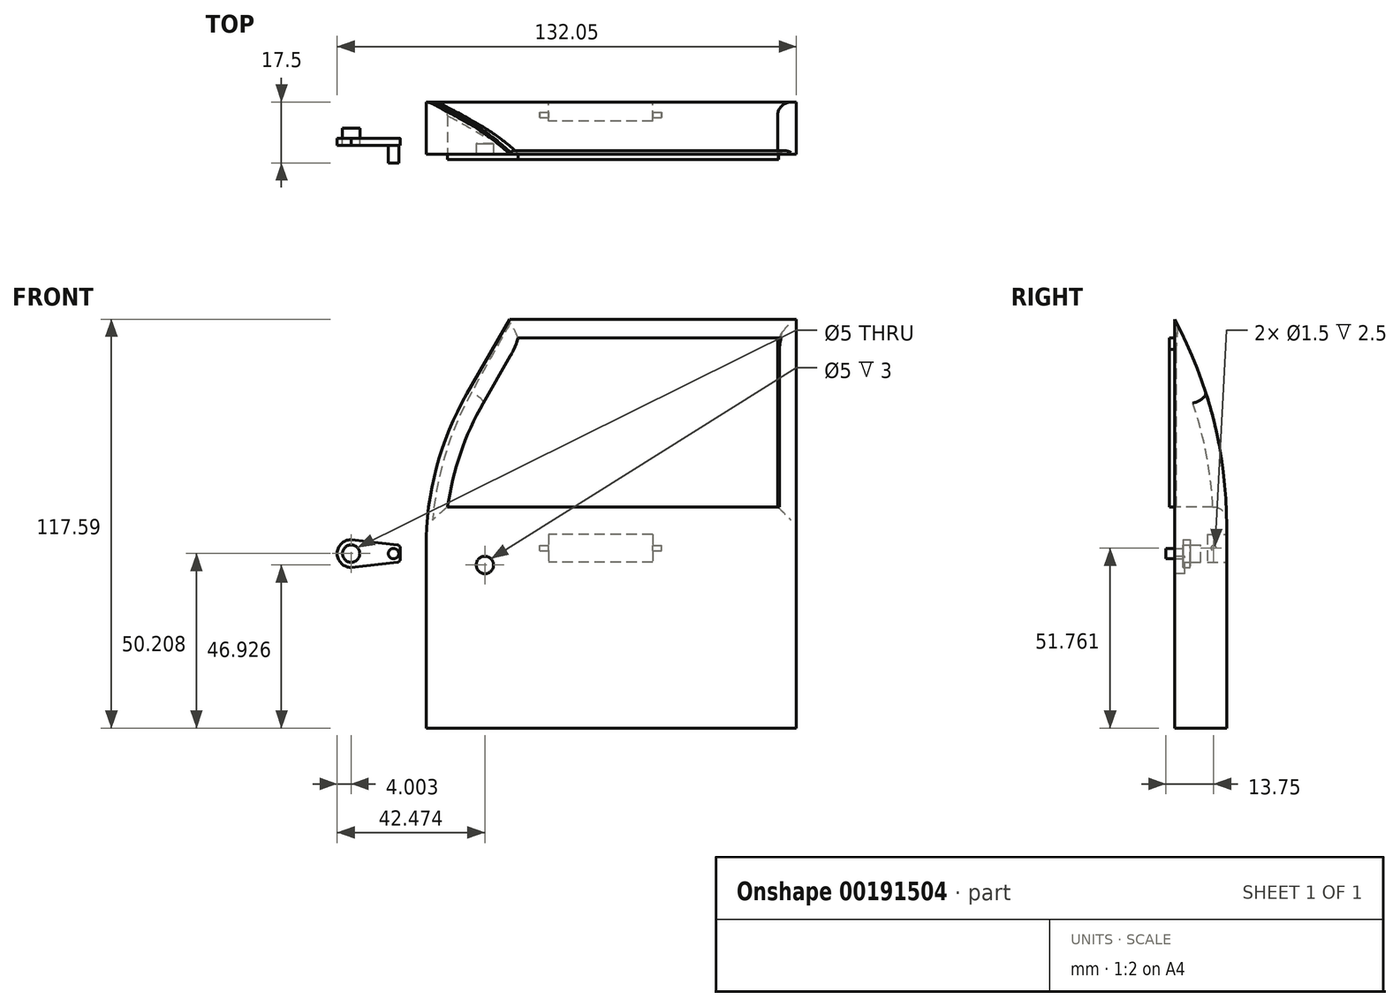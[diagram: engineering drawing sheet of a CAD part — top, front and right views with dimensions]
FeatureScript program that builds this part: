
annotation { "Feature Type Name" : "Feature", "Feature Type Description" : "" }
export const myFeature = defineFeature(function(context is Context, id is Id, definition is map)
    precondition{}
    {
        {
            var Q0;
            Q0=qCreatedBy(makeId("Front.planeOp"),FACE);
            var sketch = newSketch(context, id + "F0", { "sketchPlane" : qUnion([Q0])});
            skLineSegment(sketch, "E0.bottom", {"start": v(-26.16, 41.9) * mm, "end": v(56.28, 41.9) * mm});
            skLineSegment(sketch, "E0.right", {"start": v(56.28, 41.9) * mm, "end": v(56.28, -75.68) * mm});
            skLineSegment(sketch, "E1", {"start": v(-50.22, -75.68) * mm, "end": v(-50.22, 0) * mm});
            skLineSegment(sketch, "E2", {"start": v(-50.22, 0) * mm, "end": v(-26.16, 41.9) * mm});
            skLineSegment(sketch, "E3", {"start": v(-50.22, -75.68) * mm, "end": v(56.28, -75.68) * mm});
            skSolve(sketch);
        }
        {
            var Q0;
            Q0=makeQuery(id+"F0.imprint","IMPRINT",FACE,{"disambiguationData":[TD([[makeQuery(id+"F0.imprint","IMPRINT",EDGE,{"derivedFrom":sQuery(id+"F0.wireOp",EDGE,"E0.bottom")}),-1.0]])]});
            extrude(context, id + "F1", {"entities" : qUnion([Q0]), "endBound" : BoundingType.SYMMETRIC, "depth" : 15 * mm});
        }
        {
            var Q0;
            Q0=makeQuery(id+"F1.opExtrude","CAP_EDGE",EDGE,{"disambiguationData":[OSD([sQuery(id+"F0.wireOp",EDGE,"E0.bottom")])],"isStart":true});
            fillet(context, id + "F2", {"entities" : qUnion([Q0]), "radius" : 124.81 * mm, "tangentPropagation" : true, "allowEdgeOverflow" : false});
        }
        {
            var Q0;
            Q0=makeQuery(id+"F1.opExtrude","SWEPT_EDGE",EDGE,{"disambiguationData":[OSD([sQuery(id+"F0.wireOp",EDGE,"E1"),sQuery(id+"F0.wireOp",EDGE,"E2")])]});
            fillet(context, id + "F3", {"entities" : qUnion([Q0]), "radius" : 88.73 * mm, "tangentPropagation" : true, "allowEdgeOverflow" : false});
        }
        {
            var Q0;
            Q0=makeQuery(id+"F1.opExtrude","CAP_FACE",FACE,{"disambiguationData":[OSD([sQuery(id+"F0.wireOp",EDGE,"E0.bottom"),sQuery(id+"F0.wireOp",EDGE,"E0.right"),sQuery(id+"F0.wireOp",EDGE,"E1"),sQuery(id+"F0.wireOp",EDGE,"E2"),sQuery(id+"F0.wireOp",EDGE,"E3")])],"isStart":true});
            var sketch = newSketch(context, id + "F4", { "sketchPlane" : qUnion([Q0])});
            skSolve(sketch);
        }
        {
            var Q0;
            {var subQ0=sQuery(id+"F0.wireOp",EDGE,"E3");Q0=makeQuery(id+"F4.imprint","IMPRINT",FACE,{"disambiguationData":[TD([[makeQuery(id+"F4.imprint","IMPRINT",EDGE,{"derivedFrom":makeQuery(id+"F1.opExtrude","CAP_EDGE",EDGE,{"disambiguationData":[OSD([subQ0])],"isStart":true})}),-1.0]])]});}
            var sketch = newSketch(context, id + "F5", { "sketchPlane" : qUnion([Q0])});
            skLineSegment(sketch, "E4.bottom", {"start": v(-15, -19.92) * mm, "end": v(15, -19.92) * mm});
            skLineSegment(sketch, "E4.top", {"start": v(-15, -27.92) * mm, "end": v(15, -27.92) * mm});
            skLineSegment(sketch, "E4.left", {"start": v(-15, -19.92) * mm, "end": v(-15, -27.92) * mm});
            skLineSegment(sketch, "E4.right", {"start": v(15, -19.92) * mm, "end": v(15, -27.92) * mm});
            skPoint(sketch, "E5", {"position": v(0, -19.92) * mm});
            skSolve(sketch);
        }
        {
            var Q0;
            Q0 = qSketchRegion(id + "F5", true);
            extrude(context, id + "F6", {"entities" : qUnion([Q0]), "operationType" : NewBodyOperationType.REMOVE, "oppositeDirection" : true, "depth" : 5.5 * mm});
        }
        {
            var Q0;
            Q0=qCreatedBy(makeId("Right.planeOp"),FACE);
            var sketch = newSketch(context, id + "F7", { "sketchPlane" : qUnion([Q0])});
            skLineSegment(sketch, "E6", {"start": v(7.5, -23.92) * mm, "end": v(0, -23.92) * mm});
            skCircle(sketch, "E7", {"center": v(3.75, -23.92) * mm, "radius": 0.75 * mm});
            skSolve(sketch);
        }
        {
            var Q0;
            Q0 = qSketchRegion(id + "F7", true);
            extrude(context, id + "F8", {"entities" : qUnion([Q0]), "operationType" : NewBodyOperationType.REMOVE, "endBound" : BoundingType.SYMMETRIC, "oppositeDirection" : true, "depth" : 35 * mm});
        }
        {
            var Q0;
            Q0=qCreatedBy(makeId("Front.planeOp"),FACE);
            var sketch = newSketch(context, id + "F9", { "sketchPlane" : qUnion([Q0])});
            skArc(sketch, "E8.0", {"start": v(-44, -12.02) * mm, "mid": v(-40.3, 3.4) * mm, "end": v(-33.76, 17.83) * mm});
            skLineSegment(sketch, "E8.1", {"start": v(50.88, -12.02) * mm, "end": v(-44, -12.02) * mm});
            skLineSegment(sketch, "E8.2", {"start": v(-33.76, 17.83) * mm, "end": v(-23.03, 36.5) * mm});
            skLineSegment(sketch, "E8.3", {"start": v(-23.03, 36.5) * mm, "end": v(50.88, 36.5) * mm});
            skLineSegment(sketch, "E8.4", {"start": v(50.88, 36.5) * mm, "end": v(50.88, -12.02) * mm});
            skSolve(sketch);
        }
        {
            var Q0;
            Q0 = qSketchRegion(id + "F9", true);
            extrude(context, id + "F10", {"entities" : qUnion([Q0]), "operationType" : NewBodyOperationType.REMOVE, "endBound" : BoundingType.SYMMETRIC, "oppositeDirection" : true, "depth" : 25 * mm});
        }
        {
            var Q0;
            Q0=makeQuery(id+"F10.boolean.opBoolean","INTERSECT",EDGE,{"derivedFrom":[makeQuery(id+"F2.opFillet","BLEND_FACE",FACE,{"disambiguationData":[OSD([sQuery(id+"F0.wireOp",EDGE,"E0.bottom")])]}),makeQuery(id+"F10.opExtrude","SWEPT_FACE",FACE,{"disambiguationData":[OSD([sQuery(id+"F9.wireOp",EDGE,"E8.1")])]})]});
            var Q1;
            Q1=makeQuery(id+"F10.boolean.opBoolean","INTERSECT",EDGE,{"derivedFrom":[makeQuery(id+"F2.opFillet","BLEND_FACE",FACE,{"disambiguationData":[OSD([sQuery(id+"F0.wireOp",EDGE,"E0.bottom")])]}),makeQuery(id+"F10.opExtrude","SWEPT_FACE",FACE,{"disambiguationData":[OSD([sQuery(id+"F9.wireOp",EDGE,"E8.0")])]})]});
            var Q2;
            Q2=makeQuery(id+"F10.boolean.opBoolean","INTERSECT",EDGE,{"derivedFrom":[makeQuery(id+"F2.opFillet","BLEND_FACE",FACE,{"disambiguationData":[OSD([sQuery(id+"F0.wireOp",EDGE,"E0.bottom")])]}),makeQuery(id+"F10.opExtrude","SWEPT_FACE",FACE,{"disambiguationData":[OSD([sQuery(id+"F9.wireOp",EDGE,"E8.4")])]})]});
            var Q3;
            Q3=makeQuery(id+"F10.boolean.opBoolean","INTERSECT",EDGE,{"derivedFrom":[makeQuery(id+"F2.opFillet","BLEND_FACE",FACE,{"disambiguationData":[OSD([sQuery(id+"F0.wireOp",EDGE,"E0.bottom")])]}),makeQuery(id+"F10.opExtrude","SWEPT_FACE",FACE,{"disambiguationData":[OSD([sQuery(id+"F9.wireOp",EDGE,"E8.3")])]})]});
            fillet(context, id + "F11", {"entities" : qUnion([Q0, Q1, Q2, Q3]), "radius" : 3.86 * mm, "tangentPropagation" : true, "allowEdgeOverflow" : false});
        }
        {
            var Q0;
            Q0=makeQuery(id+"F1.opExtrude","CAP_FACE",FACE,{"disambiguationData":[OSD([sQuery(id+"F0.wireOp",EDGE,"E0.bottom"),sQuery(id+"F0.wireOp",EDGE,"E0.right"),sQuery(id+"F0.wireOp",EDGE,"E1"),sQuery(id+"F0.wireOp",EDGE,"E2"),sQuery(id+"F0.wireOp",EDGE,"E3")])],"isStart":false});
            var sketch = newSketch(context, id + "F12", { "sketchPlane" : qUnion([Q0])});
            skLineSegment(sketch, "E9.0", {"start": v(50.88, -12.02) * mm, "end": v(-44, -12.02) * mm});
            skLineSegment(sketch, "E9.1", {"start": v(50.88, 33.28) * mm, "end": v(50.88, -12.02) * mm});
            skLineSegment(sketch, "E9.2", {"start": v(-33.76, 17.83) * mm, "end": v(-26, 31.35) * mm});
            skFitSpline(sketch, "E9.3", {"points": [v(-26, 31.35) * mm, v(-25.52, 32.17) * mm, v(-24.68, 33.84) * mm, v(-24.03, 35.6) * mm, v(-23.8, 36.5) * mm]});
            skLineSegment(sketch, "E9.4", {"start": v(-23.8, 36.5) * mm, "end": v(51.14, 36.5) * mm});
            skArc(sketch, "E9.5", {"start": v(-44, -12.02) * mm, "mid": v(-40.3, 3.4) * mm, "end": v(-33.76, 17.83) * mm});
            skFitSpline(sketch, "E9.6", {"points": [v(51.14, 36.5) * mm, v(50.96, 35.44) * mm, v(50.88, 34.36) * mm, v(50.88, 33.28) * mm]});
            skSolve(sketch);
        }
        {
            var Q0;
            Q0=makeQuery(id+"F12.imprint","IMPRINT",FACE,{"disambiguationData":[TD([[makeQuery(id+"F12.imprint","IMPRINT",EDGE,{"derivedFrom":sQuery(id+"F12.wireOp",EDGE,"E9.0")}),-1.0]])]});
            extrude(context, id + "F13", {"entities" : qUnion([Q0]), "depth" : 1.5 * mm});
        }
        {
            var Q0;
            Q0=makeQuery(id+"F1.opExtrude","CAP_FACE",FACE,{"disambiguationData":[OSD([sQuery(id+"F0.wireOp",EDGE,"E0.bottom"),sQuery(id+"F0.wireOp",EDGE,"E0.right"),sQuery(id+"F0.wireOp",EDGE,"E1"),sQuery(id+"F0.wireOp",EDGE,"E2"),sQuery(id+"F0.wireOp",EDGE,"E3")])],"isStart":false});
            var sketch = newSketch(context, id + "F14", { "sketchPlane" : qUnion([Q0])});
            skCircle(sketch, "E10", {"center": v(-33.3, -28.75) * mm, "radius": 2.5 * mm});
            skSolve(sketch);
        }
        {
            var Q0;
            Q0=makeQuery(id+"F14.imprint","IMPRINT",FACE,{"disambiguationData":[TD([[makeQuery(id+"F14.imprint","IMPRINT",EDGE,{"derivedFrom":sQuery(id+"F14.wireOp",EDGE,"E10")}),1.0]])]});
            extrude(context, id + "F15", {"entities" : qUnion([Q0]), "operationType" : NewBodyOperationType.REMOVE, "oppositeDirection" : true, "depth" : 3 * mm});
        }
        {
            var Q0;
            Q0=qCreatedBy(makeId("Front.planeOp"),FACE);
            var sketch = newSketch(context, id + "F16", { "sketchPlane" : qUnion([Q0])});
            skCircle(sketch, "E11", {"center": v(-71.77, -25.47) * mm, "radius": 2.5 * mm});
            skSolve(sketch);
        }
        {
            var Q0;
            Q0=makeQuery(id+"F16.imprint","IMPRINT",FACE,{"disambiguationData":[TD([[makeQuery(id+"F16.imprint","IMPRINT",EDGE,{"derivedFrom":sQuery(id+"F16.wireOp",EDGE,"E11")}),1.0]])]});
            extrude(context, id + "F17", {"entities" : qUnion([Q0]), "depth" : 3 * mm});
        }
        {
            var Q0;
            Q0=makeQuery(id+"F17.opExtrude","CAP_FACE",FACE,{"disambiguationData":[OSD([sQuery(id+"F16.wireOp",EDGE,"E11")])],"isStart":false});
            var sketch = newSketch(context, id + "F18", { "sketchPlane" : qUnion([Q0])});
            skCircle(sketch, "E12.0", {"center": v(-71.77, -25.47) * mm, "radius": 4 * mm});
            skLineSegment(sketch, "E13", {"start": v(-71.77, -25.47) * mm, "end": v(-67.77, -25.47) * mm});
            skLineSegment(sketch, "E14", {"start": v(-67.77, -25.47) * mm, "end": v(-71.77, -25.47) * mm});
            skLineSegment(sketch, "E15", {"start": v(-75.77, -25.47) * mm, "end": v(-71.77, -25.47) * mm});
            skLineSegment(sketch, "E16", {"start": v(-71.77, -21.47) * mm, "end": v(-58.43, -22.98) * mm});
            skLineSegment(sketch, "E17", {"start": v(-57.64, -23.87) * mm, "end": v(-57.64, -25.47) * mm});
            skLineSegment(sketch, "E18", {"start": v(-57.64, -25.47) * mm, "end": v(-67.77, -25.47) * mm});
            skPoint(sketch, "E19.visualSharp", {"position": v(-57.64, -23.07) * mm});
            skArc(sketch, "E19.filletArc", {"start": v(-57.64, -23.87) * mm, "mid": v(-57.87, -23.27) * mm, "end": v(-58.43, -22.98) * mm});
            skLineSegment(sketch, "E20.MirrorCS", {"start": v(-71.77, -29.47) * mm, "end": v(-58.43, -27.97) * mm});
            skLineSegment(sketch, "E21.MirrorCS", {"start": v(-57.64, -27.08) * mm, "end": v(-57.64, -25.47) * mm});
            skArc(sketch, "E22.MirrorCS", {"start": v(-57.64, -27.08) * mm, "mid": v(-57.87, -27.67) * mm, "end": v(-58.43, -27.97) * mm});
            skSolve(sketch);
        }
        {
            var Q0;
            Q0=makeQuery(id+"F18.imprint","IMPRINT",FACE,{"disambiguationData":[TD([[makeQuery(id+"F18.imprint","IMPRINT",EDGE,{"derivedFrom":sQuery(id+"F18.wireOp",EDGE,"E17")}),-1.0]])]});
            var Q1;
            {var subQ0=sQuery(id+"F18.wireOp",EDGE,"E15");var subQ1=sQuery(id+"F18.wireOp",EDGE,"E12.0");var subQ2=makeQuery(id+"F18.imprint","INTERSECT",VERTEX,{"derivedFrom":[subQ1,subQ0]});Q1=makeQuery(id+"F18.imprint","IMPRINT",FACE,{"disambiguationData":[TD([[makeQuery(id+"F18.imprint","IMPRINT",EDGE,{"disambiguationData":[TD([[subQ2,1.0]])],"derivedFrom":subQ1}),1.0]])]});}
            var Q2;
            {var subQ0=sQuery(id+"F18.wireOp",EDGE,"E15");var subQ1=sQuery(id+"F18.wireOp",EDGE,"E14");var subQ2=makeQuery(id+"F18.imprint","INTERSECT",VERTEX,{"derivedFrom":[subQ1,subQ0]});Q2=makeQuery(id+"F18.imprint","IMPRINT",FACE,{"disambiguationData":[TD([[makeQuery(id+"F18.imprint","IMPRINT",EDGE,{"disambiguationData":[TD([[subQ2,1.0]])],"derivedFrom":subQ1}),-1.0]])]});}
            var Q3;
            {var subQ0=sQuery(id+"F18.wireOp",EDGE,"E15");var subQ1=sQuery(id+"F18.wireOp",EDGE,"E14");var subQ2=makeQuery(id+"F18.imprint","INTERSECT",VERTEX,{"derivedFrom":[subQ1,subQ0]});Q3=makeQuery(id+"F18.imprint","IMPRINT",FACE,{"disambiguationData":[TD([[makeQuery(id+"F18.imprint","IMPRINT",EDGE,{"disambiguationData":[TD([[subQ2,1.0]])],"derivedFrom":subQ1}),1.0]])]});}
            var Q4;
            {var subQ0=sQuery(id+"F18.wireOp",EDGE,"E15");var subQ1=sQuery(id+"F18.wireOp",EDGE,"E12.0");var subQ2=makeQuery(id+"F18.imprint","INTERSECT",VERTEX,{"derivedFrom":[subQ1,subQ0]});Q4=makeQuery(id+"F18.imprint","IMPRINT",FACE,{"disambiguationData":[TD([[makeQuery(id+"F18.imprint","IMPRINT",EDGE,{"disambiguationData":[TD([[subQ2,-1.0]])],"derivedFrom":subQ1}),1.0]])]});}
            var Q5;
            {var subQ4=sQuery(id+"F18.wireOp",EDGE,"E18");Q5=makeQuery(id+"F18.imprint","IMPRINT",FACE,{"disambiguationData":[TD([[makeQuery(id+"F18.imprint","IMPRINT",EDGE,{"derivedFrom":subQ4}),1.0]])]});}
            extrude(context, id + "F19", {"entities" : qUnion([Q0, Q1, Q2, Q3, Q4, Q5]), "operationType" : NewBodyOperationType.ADD, "depth" : 2 * mm});
        }
        {
            var Q0;
            Q0=makeQuery(id+"F19.opExtrude","CAP_FACE",FACE,{"disambiguationData":[OSD([sQuery(id+"F18.wireOp",EDGE,"E12.0"),sQuery(id+"F18.wireOp",EDGE,"E16"),sQuery(id+"F18.wireOp",EDGE,"E17"),sQuery(id+"F18.wireOp",EDGE,"E19.filletArc"),sQuery(id+"F18.wireOp",EDGE,"E20.MirrorCS"),sQuery(id+"F18.wireOp",EDGE,"E21.MirrorCS"),sQuery(id+"F18.wireOp",EDGE,"E22.MirrorCS")])],"isStart":false});
            var sketch = newSketch(context, id + "F20", { "sketchPlane" : qUnion([Q0])});
            skLineSegment(sketch, "E23", {"start": v(-59.57, -22.85) * mm, "end": v(-59.57, -28.1) * mm});
            skCircle(sketch, "E24", {"center": v(-59.57, -25.47) * mm, "radius": 1.5 * mm});
            skSolve(sketch);
        }
        {
            var Q0;
            {var subQ0=sQuery(id+"F20.wireOp",EDGE,"NAi4OqM0-GqMM-OB6Y-wDg8-DC8Bh4hhFyPi");var subQ1=sQuery(id+"F20.wireOp",EDGE,"UeGyKsjW-u3MC-qCC2-V1O2-ia5C01j86NAJ");var subQ2=makeQuery(id+"F20.imprint","INTERSECT",VERTEX,{"disambiguationData":[OD(0.0)],"derivedFrom":[subQ1,subQ0]});Q0=makeQuery(id+"F20.imprint","IMPRINT",FACE,{"disambiguationData":[TD([[makeQuery(id+"F20.imprint","IMPRINT",EDGE,{"disambiguationData":[TD([[subQ2,-1.0]])],"derivedFrom":subQ1}),-1.0]])]});}
            var Q1;
            {var subQ0=sQuery(id+"F20.wireOp",EDGE,"NAi4OqM0-GqMM-OB6Y-wDg8-DC8Bh4hhFyPi");var subQ1=sQuery(id+"F20.wireOp",EDGE,"UeGyKsjW-u3MC-qCC2-V1O2-ia5C01j86NAJ");var subQ2=makeQuery(id+"F20.imprint","INTERSECT",VERTEX,{"disambiguationData":[OD(0.0)],"derivedFrom":[subQ1,subQ0]});Q1=makeQuery(id+"F20.imprint","IMPRINT",FACE,{"disambiguationData":[TD([[makeQuery(id+"F20.imprint","IMPRINT",EDGE,{"disambiguationData":[TD([[subQ2,-1.0]])],"derivedFrom":subQ1}),1.0]])]});}
            var Q2;
            {var subQ0=sQuery(id+"F20.wireOp",EDGE,"E24");var subQ1=sQuery(id+"F20.wireOp",EDGE,"E23");var subQ2=makeQuery(id+"F20.imprint","INTERSECT",VERTEX,{"disambiguationData":[OD(0.0)],"derivedFrom":[subQ1,subQ0]});Q2=makeQuery(id+"F20.imprint","IMPRINT",FACE,{"disambiguationData":[TD([[makeQuery(id+"F20.imprint","IMPRINT",EDGE,{"disambiguationData":[TD([[subQ2,-1.0]])],"derivedFrom":subQ1}),-1.0]])]});}
            var Q3;
            {var subQ0=sQuery(id+"F20.wireOp",EDGE,"E24");var subQ1=sQuery(id+"F20.wireOp",EDGE,"E23");var subQ2=makeQuery(id+"F20.imprint","INTERSECT",VERTEX,{"disambiguationData":[OD(0.0)],"derivedFrom":[subQ1,subQ0]});Q3=makeQuery(id+"F20.imprint","IMPRINT",FACE,{"disambiguationData":[TD([[makeQuery(id+"F20.imprint","IMPRINT",EDGE,{"disambiguationData":[TD([[subQ2,-1.0]])],"derivedFrom":subQ1}),1.0]])]});}
            extrude(context, id + "F21", {"entities" : qUnion([Q0, Q1, Q2, Q3]), "operationType" : NewBodyOperationType.ADD, "depth" : 5 * mm});
        }
        {
            var Q0;
            Q0=makeQuery(id+"F10.boolean.opBoolean","INTERSECT",EDGE,{"derivedFrom":[makeQuery(id+"F1.opExtrude","CAP_FACE",FACE,{"disambiguationData":[OSD([sQuery(id+"F0.wireOp",EDGE,"E0.bottom"),sQuery(id+"F0.wireOp",EDGE,"E0.right"),sQuery(id+"F0.wireOp",EDGE,"E1"),sQuery(id+"F0.wireOp",EDGE,"E2"),sQuery(id+"F0.wireOp",EDGE,"E3")])],"isStart":false}),makeQuery(id+"F10.opExtrude","SWEPT_FACE",FACE,{"disambiguationData":[OSD([sQuery(id+"F9.wireOp",EDGE,"E8.4")])]})]});
            chamfer(context, id + "F22", {"entities" : qUnion([Q0]), "width" : 0.5 * mm, "tangentPropagation" : true});
        }
    });
